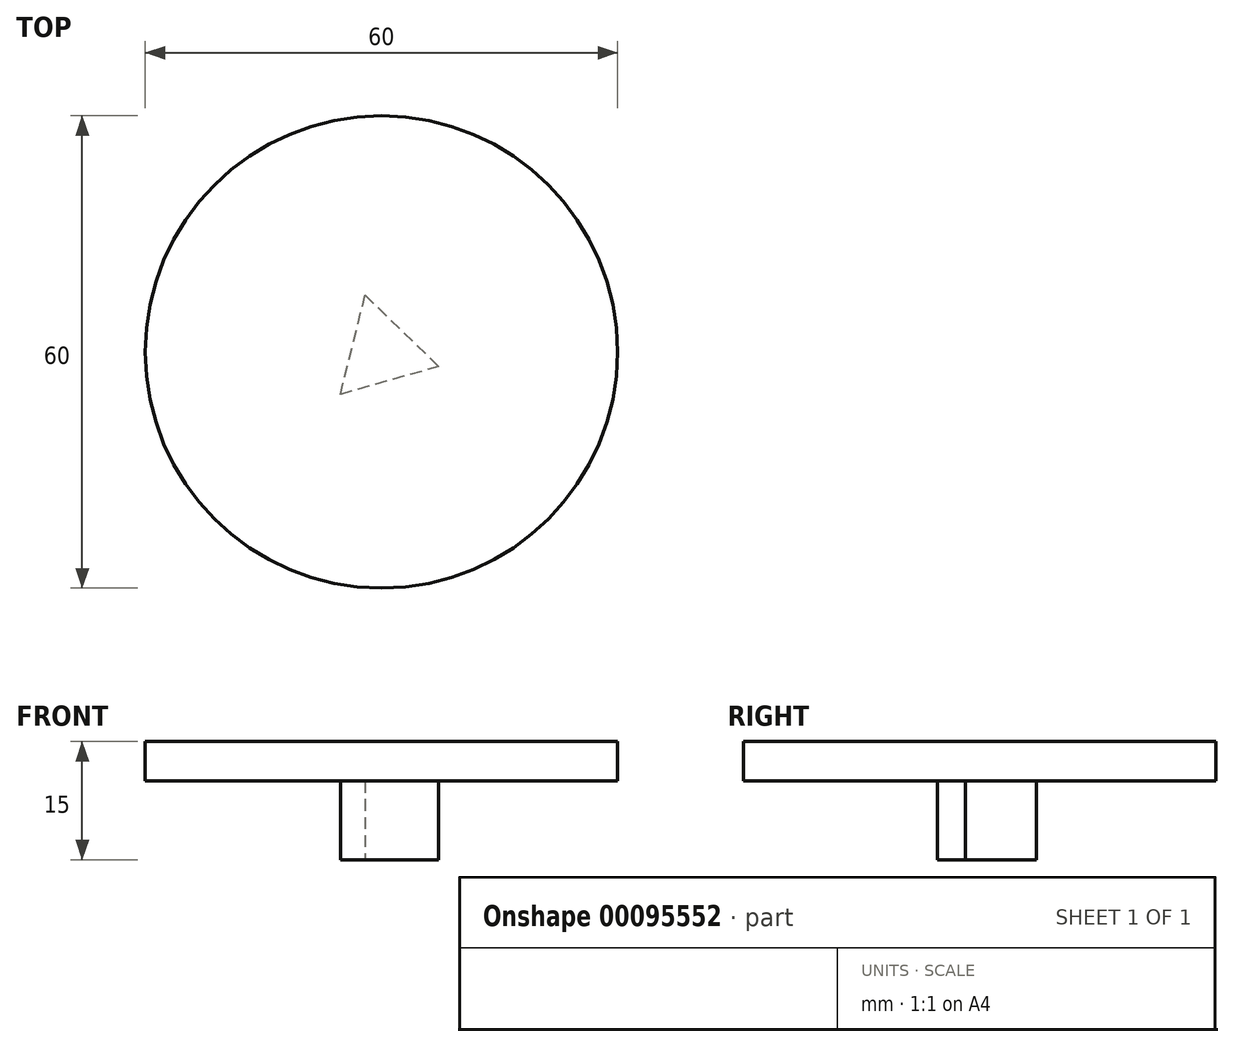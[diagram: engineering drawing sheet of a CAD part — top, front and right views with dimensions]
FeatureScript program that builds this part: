
annotation { "Feature Type Name" : "Feature", "Feature Type Description" : "" }
export const myFeature = defineFeature(function(context is Context, id is Id, definition is map)
    precondition{}
    {
        {
            var Q0;
            Q0=qCreatedBy(makeId("Top.planeOp"),FACE);
            var sketch = newSketch(context, id + "F0", { "sketchPlane" : qUnion([Q0])});
            skCircle(sketch, "E0.cCircle", {"center": v(0, 0) * mm, "radius": 7.5 * mm, "construction": true});
            skLineSegment(sketch, "E0.0", {"start": v(-5.22, -5.4) * mm, "end": v(-2.06, 7.22) * mm});
            skLineSegment(sketch, "E0.1", {"start": v(-2.06, 7.22) * mm, "end": v(7.28, -1.82) * mm});
            skLineSegment(sketch, "E0.2", {"start": v(7.28, -1.82) * mm, "end": v(-5.22, -5.4) * mm});
            skSolve(sketch);
        }
        {
            var Q0;
            Q0 = qSketchRegion(id + "F0", true);
            extrude(context, id + "F1", {"entities" : qUnion([Q0]), "depth" : 10 * mm});
        }
        {
            var Q0;
            Q0=makeQuery(id+"F1.opExtrude","CAP_FACE",FACE,{"disambiguationData":[OSD([sQuery(id+"F0.wireOp",EDGE,"E0.0"),sQuery(id+"F0.wireOp",EDGE,"E0.1"),sQuery(id+"F0.wireOp",EDGE,"E0.2")])],"isStart":false});
            var sketch = newSketch(context, id + "F2", { "sketchPlane" : qUnion([Q0])});
            skCircle(sketch, "E1", {"center": v(0, 0) * mm, "radius": 30 * mm});
            skSolve(sketch);
        }
        {
            var Q0;
            Q0 = qSketchRegion(id + "F2", true);
            extrude(context, id + "F3", {"entities" : qUnion([Q0]), "operationType" : NewBodyOperationType.ADD, "depth" : 5 * mm});
        }
    });
